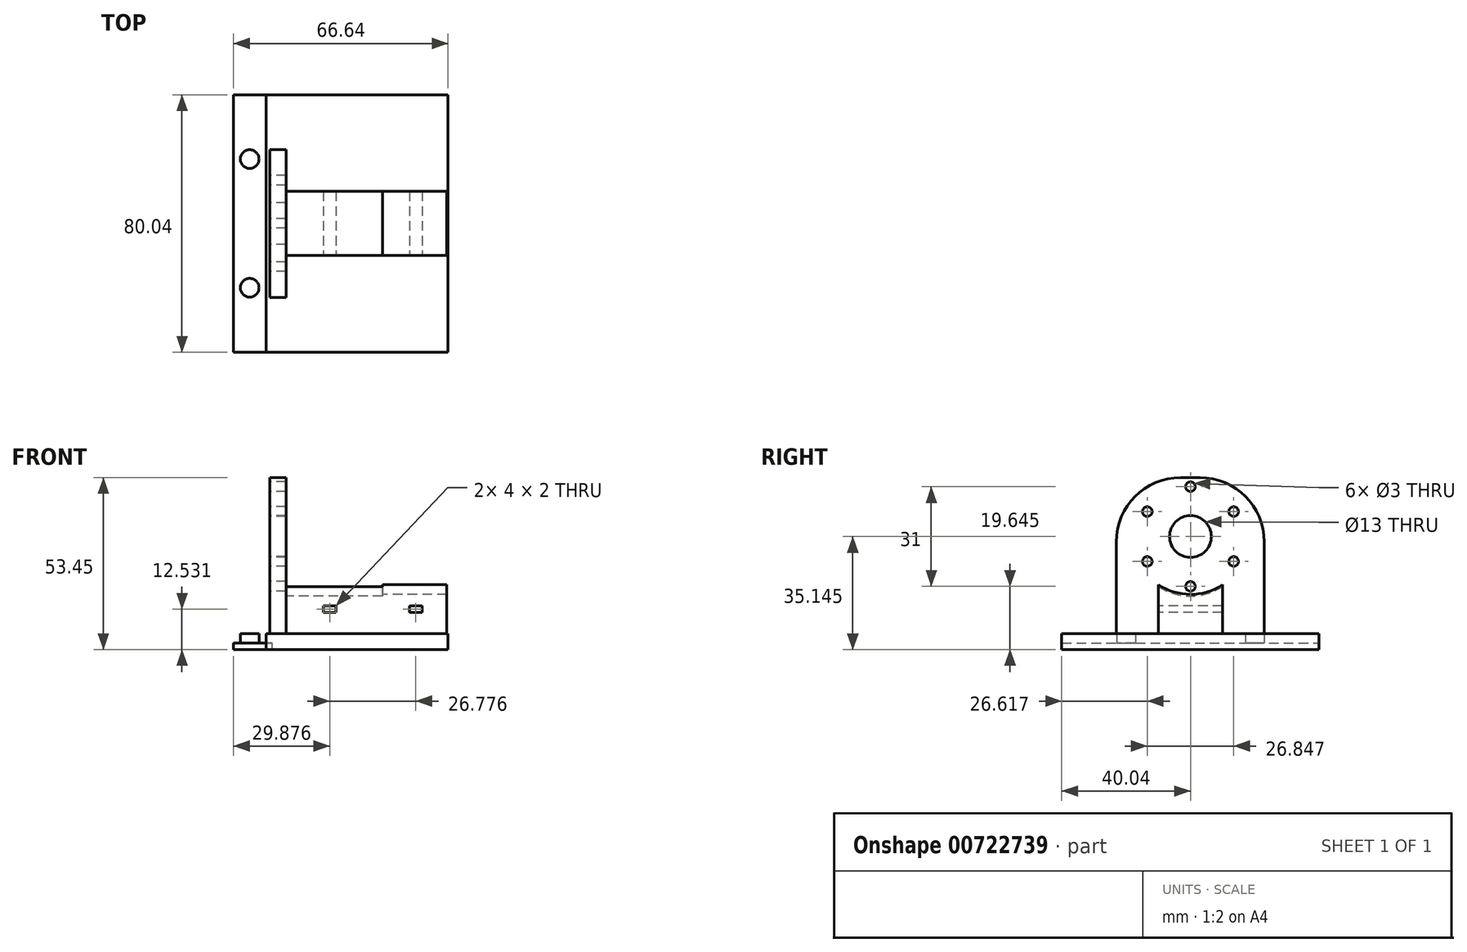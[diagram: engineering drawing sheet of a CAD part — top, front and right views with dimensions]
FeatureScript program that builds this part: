
annotation { "Feature Type Name" : "Feature", "Feature Type Description" : "" }
export const myFeature = defineFeature(function(context is Context, id is Id, definition is map)
    precondition{}
    {
        {
            var Q0;
            Q0=qCreatedBy(makeId("Top.planeOp"),FACE);
            var sketch = newSketch(context, id + "F0", { "sketchPlane" : qUnion([Q0])});
            skLineSegment(sketch, "E0.bottom", {"start": v(-31.3, -40) * mm, "end": v(-41.3, -40) * mm});
            skLineSegment(sketch, "E0.top", {"start": v(-31.3, 40) * mm, "end": v(-41.3, 40) * mm});
            skLineSegment(sketch, "E0.right", {"start": v(-41.3, -40) * mm, "end": v(-41.3, 40) * mm});
            skPoint(sketch, "E0.middle", {"position": v(-36.3, 0) * mm});
            skLineSegment(sketch, "E1", {"start": v(-31.3, 40) * mm, "end": v(-29.3, 40) * mm});
            skLineSegment(sketch, "E2", {"start": v(-29.3, 40) * mm, "end": v(-29.3, -40) * mm});
            skLineSegment(sketch, "E3", {"start": v(-29.3, -40) * mm, "end": v(-31.3, -40) * mm});
            skLineSegment(sketch, "E4", {"start": v(-27.78, 0) * mm, "end": v(-27.78, 41.64) * mm, "construction": true});
            skLineSegment(sketch, "E5", {"start": v(-27.78, 41.64) * mm, "end": v(-43.97, 41.64) * mm, "construction": true});
            skSolve(sketch);
        }
        {
            var Q0;
            Q0 = qSketchRegion(id + "F0", true);
            extrude(context, id + "F1", {"entities" : qUnion([Q0]), "depth" : 2 * mm, "offsetDistance" : 25 * mm});
        }
        {
            var Q0;
            Q0=makeQuery(id+"F1.opExtrude","CAP_FACE",FACE,{"disambiguationData":[OSD([sQuery(id+"F0.wireOp",EDGE,"E0.bottom"),sQuery(id+"F0.wireOp",EDGE,"E0.top"),sQuery(id+"F0.wireOp",EDGE,"E0.left"),sQuery(id+"F0.wireOp",EDGE,"E0.right")])],"isStart":false});
            var sketch = newSketch(context, id + "F2", { "sketchPlane" : qUnion([Q0])});
            skLineSegment(sketch, "E6", {"start": v(-31.3, 0) * mm, "end": v(-36.3, 0) * mm, "construction": true});
            skLineSegment(sketch, "E7", {"start": v(-36.3, 0) * mm, "end": v(-36.3, -20) * mm, "construction": true});
            skCircle(sketch, "E8", {"center": v(-36.3, -20) * mm, "radius": 2.9 * mm});
            skSolve(sketch);
        }
        {
            var Q0;
            Q0=makeQuery(id+"F2.imprint","IMPRINT",FACE,{"disambiguationData":[TD([[makeQuery(id+"F2.imprint","IMPRINT",EDGE,{"derivedFrom":sQuery(id+"F2.wireOp",EDGE,"E8")}),1.0]])]});
            extrude(context, id + "F3", {"entities" : qUnion([Q0]), "depth" : 3 * mm, "offsetDistance" : 25 * mm});
        }
        {
            var Q0;
            Q0=makeQuery(id+"F3.opExtrude","SWEPT_BODY",BODY,{"disambiguationData":[OSD([sQuery(id+"F2.wireOp",EDGE,"E8")])]});
            var Q1;
            Q1=qCreatedBy(makeId("Front.planeOp"),FACE);
            mirror(context, id + "F4", {"operationType" : NewBodyOperationType.ADD, "entities" : qUnion([Q0]), "mirrorPlane" : qUnion([Q1])});
        }
        {
            var Q0;
            Q0=qCreatedBy(makeId("Top.planeOp"),FACE);
            var sketch = newSketch(context, id + "F5", { "sketchPlane" : qUnion([Q0])});
            skLineSegment(sketch, "E9.bottom", {"start": v(-31.16, 39.96) * mm, "end": v(25.34, 39.96) * mm});
            skLineSegment(sketch, "E9.top", {"start": v(-31.16, -40.04) * mm, "end": v(25.34, -40.04) * mm});
            skLineSegment(sketch, "E9.left", {"start": v(-31.16, 39.96) * mm, "end": v(-31.16, -40.04) * mm});
            skLineSegment(sketch, "E9.right", {"start": v(25.34, 39.96) * mm, "end": v(25.34, -40.04) * mm});
            skSolve(sketch);
        }
        {
            var Q0;
            Q0 = qSketchRegion(id + "F5", true);
            extrude(context, id + "F6", {"entities" : qUnion([Q0]), "operationType" : NewBodyOperationType.ADD, "depth" : 5 * mm, "offsetDistance" : 25 * mm});
        }
        {
            var Q0;
            Q0=qCreatedBy(makeId("Right.planeOp"),FACE);
            cPlane(context, id + "F7", {"entities" : qUnion([Q0]), "cplaneType" : CPlaneType.OFFSET, "offset" : 30 * mm, "oppositeDirection" : true, "width" : 150 * mm, "height" : 150 * mm});
        }
        {
            var Q0;
            Q0=qCreatedBy(id+"F7.planeOp",FACE);
            var sketch = newSketch(context, id + "F8", { "sketchPlane" : qUnion([Q0])});
            skLineSegment(sketch, "E10", {"start": v(0, 5.02) * mm, "end": v(0, 35.15) * mm, "construction": true});
            skCircle(sketch, "E11", {"center": v(0, 35.15) * mm, "radius": 6.5 * mm});
            skCircle(sketch, "E12", {"center": v(0, 35.15) * mm, "radius": 18.5 * mm, "construction": true});
            skCircle(sketch, "E13", {"center": v(0, 35.15) * mm, "radius": 15.5 * mm, "construction": true});
            skCircle(sketch, "E14", {"center": v(0, 50.65) * mm, "radius": 1.5 * mm});
            skLineSegment(sketch, "E15", {"start": v(0, 35.15) * mm, "end": v(-18.7, 35.15) * mm, "construction": true});
            skLineSegment(sketch, "E16", {"start": v(0, 35.15) * mm, "end": v(-15.81, 44.27) * mm, "construction": true});
            skLineSegment(sketch, "E17", {"start": v(0, 35.15) * mm, "end": v(19.07, 35.15) * mm, "construction": true});
            skLineSegment(sketch, "E18", {"start": v(0, 35.15) * mm, "end": v(14.9, 43.75) * mm, "construction": true});
            skCircle(sketch, "E19", {"center": v(13.42, 42.9) * mm, "radius": 1.5 * mm});
            skCircle(sketch, "E20", {"center": v(-13.42, 42.9) * mm, "radius": 1.5 * mm});
            skLineSegment(sketch, "E21.bottom", {"start": v(22.92, 5) * mm, "end": v(-23.05, 5) * mm});
            skLineSegment(sketch, "E21.left", {"start": v(22.92, 5) * mm, "end": v(22.92, 53.45) * mm});
            skLineSegment(sketch, "E21.right", {"start": v(-23.05, 5) * mm, "end": v(-23.05, 53.45) * mm});
            skLineSegment(sketch, "E22", {"start": v(0, 35.15) * mm, "end": v(17.65, 24.95) * mm, "construction": true});
            skLineSegment(sketch, "E23", {"start": v(0, 35.15) * mm, "end": v(-14.47, 26.8) * mm, "construction": true});
            skCircle(sketch, "E24", {"center": v(13.42, 27.4) * mm, "radius": 1.5 * mm});
            skCircle(sketch, "E25", {"center": v(0, 19.65) * mm, "radius": 1.5 * mm});
            skCircle(sketch, "E26", {"center": v(-13.42, 27.4) * mm, "radius": 1.5 * mm});
            skLineSegment(sketch, "E27", {"start": v(22.92, 53.45) * mm, "end": v(-23.05, 53.45) * mm, "construction": true});
            skLineSegment(sketch, "E28", {"start": v(22.92, 53.45) * mm, "end": v(-23.05, 53.45) * mm});
            skSolve(sketch);
        }
        {
            var Q0;
            Q0 = qSketchRegion(id + "F8", true);
            extrude(context, id + "F9", {"entities" : qUnion([Q0]), "depth" : 5 * mm, "offsetDistance" : 25 * mm});
        }
        {
            var Q0;
            Q0=makeQuery(id+"F9.opExtrude","CAP_FACE",FACE,{"disambiguationData":[OSD([sQuery(id+"F8.wireOp",EDGE,"E11"),sQuery(id+"F8.wireOp",EDGE,"E14"),sQuery(id+"F8.wireOp",EDGE,"E19"),sQuery(id+"F8.wireOp",EDGE,"E20"),sQuery(id+"F8.wireOp",EDGE,"E21.bottom"),sQuery(id+"F8.wireOp",EDGE,"E21.top"),sQuery(id+"F8.wireOp",EDGE,"E21.left"),sQuery(id+"F8.wireOp",EDGE,"E21.right"),sQuery(id+"F8.wireOp",EDGE,"E24"),sQuery(id+"F8.wireOp",EDGE,"E25"),sQuery(id+"F8.wireOp",EDGE,"E26")])],"isStart":false});
            var sketch = newSketch(context, id + "F10", { "sketchPlane" : qUnion([Q0])});
            skLineSegment(sketch, "E29", {"start": v(0, 5) * mm, "end": v(0, 35.15) * mm, "construction": true});
            skCircle(sketch, "E30", {"center": v(0, 35.15) * mm, "radius": 18 * mm, "construction": true});
            skLineSegment(sketch, "E31", {"start": v(-10, 5) * mm, "end": v(-10, 20.18) * mm});
            skLineSegment(sketch, "E32", {"start": v(9.96, 5) * mm, "end": v(9.96, 20.15) * mm});
            skArc(sketch, "E33", {"start": v(-10, 20.18) * mm, "mid": v(-0.03, 17.15) * mm, "end": v(9.96, 20.15) * mm});
            skLineSegment(sketch, "E34", {"start": v(-10, 5) * mm, "end": v(9.96, 5) * mm});
            skSolve(sketch);
        }
        {
            var Q0;
            Q0 = qSketchRegion(id + "F10", true);
            extrude(context, id + "F11", {"entities" : qUnion([Q0]), "depth" : 50 * mm, "offsetDistance" : 25 * mm});
        }
        {
            var Q0;
            Q0=makeQuery(id+"F9.opExtrude","CAP_FACE",FACE,{"disambiguationData":[OSD([sQuery(id+"F8.wireOp",EDGE,"E11"),sQuery(id+"F8.wireOp",EDGE,"E14"),sQuery(id+"F8.wireOp",EDGE,"E19"),sQuery(id+"F8.wireOp",EDGE,"E20"),sQuery(id+"F8.wireOp",EDGE,"E21.bottom"),sQuery(id+"F8.wireOp",EDGE,"E21.top"),sQuery(id+"F8.wireOp",EDGE,"E21.left"),sQuery(id+"F8.wireOp",EDGE,"E21.right"),sQuery(id+"F8.wireOp",EDGE,"E24"),sQuery(id+"F8.wireOp",EDGE,"E25"),sQuery(id+"F8.wireOp",EDGE,"E26")])],"isStart":false});
            var sketch = newSketch(context, id + "F12", { "sketchPlane" : qUnion([Q0])});
            skLineSegment(sketch, "E35", {"start": v(0, 5) * mm, "end": v(0, 35.12) * mm, "construction": true});
            skCircle(sketch, "E36", {"center": v(0, 35.12) * mm, "radius": 18.5 * mm});
            skCircle(sketch, "E37", {"center": v(0, 35.12) * mm, "radius": 17.5 * mm});
            skSolve(sketch);
        }
        {
            var Q0;
            Q0 = qSketchRegion(id + "F12", true);
            extrude(context, id + "F13", {"entities" : qUnion([Q0]), "operationType" : NewBodyOperationType.REMOVE, "depth" : 30 * mm, "offsetDistance" : 25 * mm});
        }
        {
            var Q0;
            Q0=makeQuery(id+"F9.opExtrude","SWEPT_EDGE",EDGE,{"disambiguationData":[OSD([sQuery(id+"F8.wireOp",EDGE,"E21.left"),sQuery(id+"F8.wireOp",EDGE,"E28")])]});
            var Q1;
            Q1=makeQuery(id+"F9.opExtrude","SWEPT_EDGE",EDGE,{"disambiguationData":[OSD([sQuery(id+"F8.wireOp",EDGE,"E21.right"),sQuery(id+"F8.wireOp",EDGE,"E28")])]});
            fillet(context, id + "F14", {"entities" : qUnion([Q0, Q1]), "radius" : 20 * mm, "tangentPropagation" : true, "allowEdgeOverflow" : false});
        }
        {
            var Q0;
            Q0=makeQuery(id+"F11.opExtrude","SWEPT_FACE",FACE,{"disambiguationData":[OSD([sQuery(id+"F10.wireOp",EDGE,"E31")])]});
            var sketch = newSketch(context, id + "F15", { "sketchPlane" : qUnion([Q0])});
            skLineSegment(sketch, "E38.bottom", {"start": v(-13.42, 13.53) * mm, "end": v(-9.42, 13.53) * mm});
            skLineSegment(sketch, "E38.top", {"start": v(-13.42, 11.53) * mm, "end": v(-9.42, 11.53) * mm});
            skLineSegment(sketch, "E38.left", {"start": v(-13.42, 13.53) * mm, "end": v(-13.42, 11.53) * mm});
            skLineSegment(sketch, "E38.right", {"start": v(-9.42, 13.53) * mm, "end": v(-9.42, 11.53) * mm});
            skLineSegment(sketch, "E39", {"start": v(-13.42, 11.53) * mm, "end": v(22.91, 11.53) * mm, "construction": true});
            skLineSegment(sketch, "E40.bottom", {"start": v(13.35, 11.53) * mm, "end": v(17.35, 11.53) * mm});
            skLineSegment(sketch, "E40.top", {"start": v(13.35, 13.53) * mm, "end": v(17.35, 13.53) * mm});
            skLineSegment(sketch, "E40.left", {"start": v(13.35, 11.53) * mm, "end": v(13.35, 13.53) * mm});
            skLineSegment(sketch, "E40.right", {"start": v(17.35, 11.53) * mm, "end": v(17.35, 13.53) * mm});
            skSolve(sketch);
        }
        {
            var Q0;
            Q0 = qSketchRegion(id + "F15", true);
            extrude(context, id + "F16", {"entities" : qUnion([Q0]), "operationType" : NewBodyOperationType.REMOVE, "oppositeDirection" : true, "depth" : 25 * mm, "offsetDistance" : 25 * mm});
        }
    });
